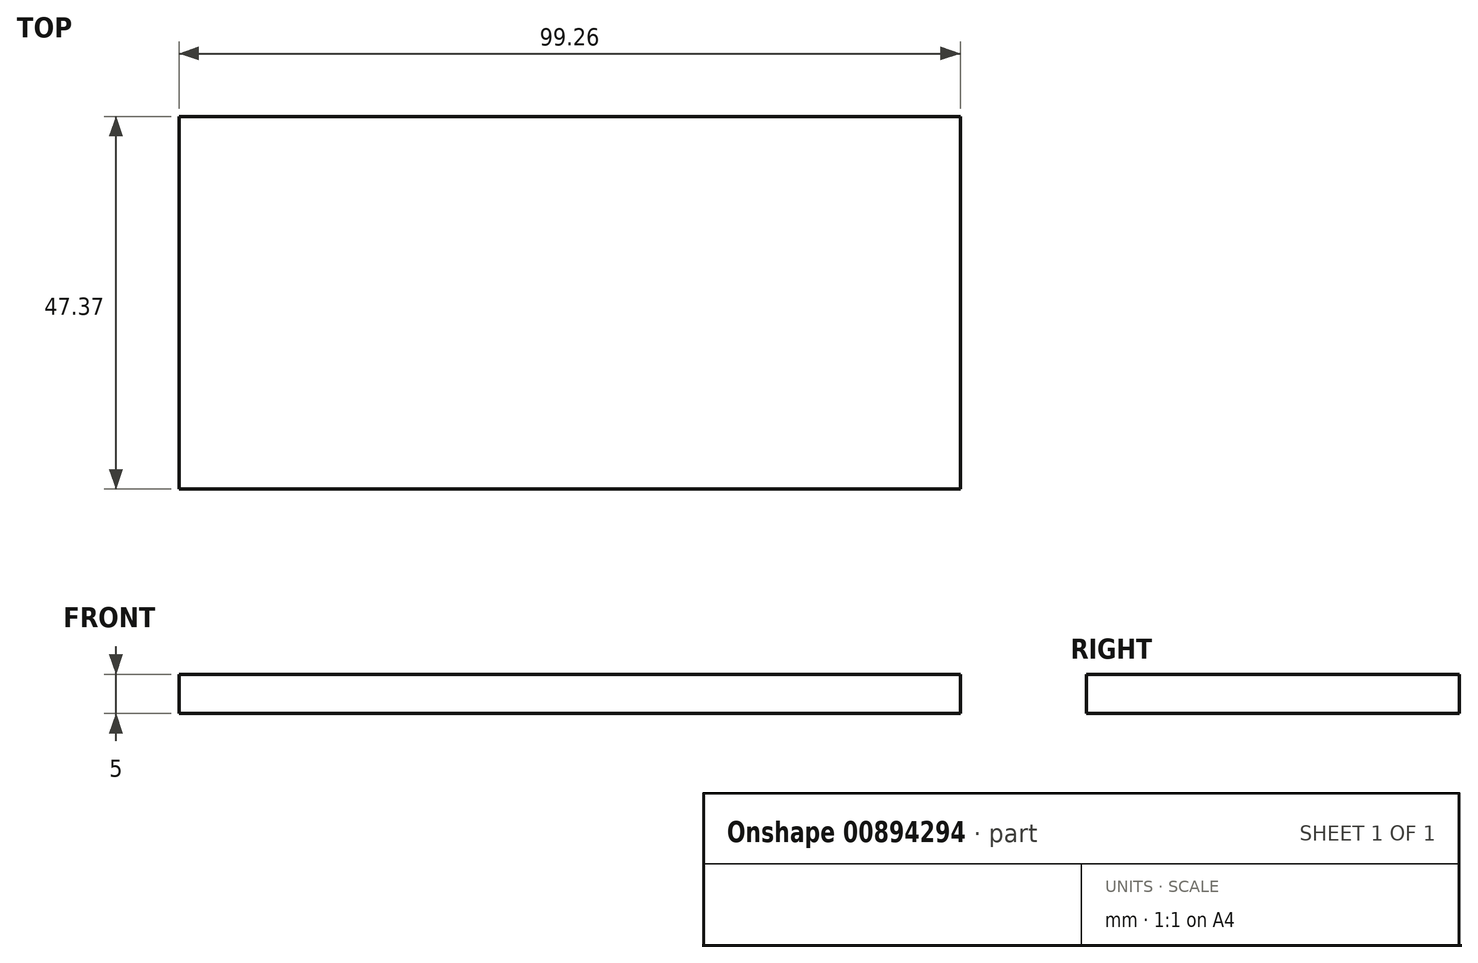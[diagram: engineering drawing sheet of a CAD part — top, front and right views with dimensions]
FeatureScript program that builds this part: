
annotation { "Feature Type Name" : "Feature", "Feature Type Description" : "" }
export const myFeature = defineFeature(function(context is Context, id is Id, definition is map)
    precondition{}
    {
        {
            var Q0;
            Q0=qCreatedBy(makeId("Top.planeOp"),FACE);
            var sketch = newSketch(context, id + "F0", { "sketchPlane" : qUnion([Q0])});
            skLineSegment(sketch, "E0.bottom", {"start": v(-60.88, -26.87) * mm, "end": v(38.38, -26.87) * mm});
            skLineSegment(sketch, "E0.top", {"start": v(-60.88, 20.5) * mm, "end": v(38.38, 20.5) * mm});
            skLineSegment(sketch, "E0.left", {"start": v(-60.88, -26.87) * mm, "end": v(-60.88, 20.5) * mm});
            skLineSegment(sketch, "E0.right", {"start": v(38.38, -26.87) * mm, "end": v(38.38, 20.5) * mm});
            skSolve(sketch);
        }
        {
            var Q0;
            Q0=makeQuery(id+"F0.imprint","IMPRINT",FACE,{"disambiguationData":[TD([[makeQuery(id+"F0.imprint","IMPRINT",EDGE,{"derivedFrom":sQuery(id+"F0.wireOp",EDGE,"E0.bottom")}),1.0]])]});
            extrude(context, id + "F1", {"entities" : qUnion([Q0]), "depth" : 5 * mm, "offsetDistance" : 25 * mm});
        }
    });
